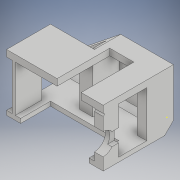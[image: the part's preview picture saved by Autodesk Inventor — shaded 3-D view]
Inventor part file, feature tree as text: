
AUTODESK INVENTOR PART (.ipt)
format: ipt  version: 2018 (Build 220112000, 112)  size: 257,024 bytes
history: native  units: in
note: dims shown in document units (in); Inventor stores cm internally (conversion verified against a paired STEP export)
features: extrude x12, sketch x12, projected_geometry x2
ambient origin geometry x8: Origin, YZ Plane, XZ Plane, XY Plane, X Axis, Y Axis, Z Axis, Center Point
bodies: Solid1 (feature_tree)
feature tree (26):
  extrude  "Extrusion1"  Depth=2.5591in
  extrude  "Extrusion2"  Depth=0.4921in
  sketch  "Sketch3"  dims[d5=0.2953in d6=0.1969in]
  extrude  "Extrusion4"  Depth=0.1969in
  extrude  "Extrusion5"  Depth=0.2953in
  sketch  "Sketch7"  dims[d11=4.3307in d12=0.0in d13=3.937in]
  extrude  "Extrusion6"  Depth=0.3937in
  extrude  "Extrusion7"  Depth=3.937in
  extrude  "Extrusion8"  Depth=1.1811in TaperAngle=0.0deg
  sketch  "Sketch9"  dims[d14=2.0669in d15=1.1811in d16=0.0in]
  extrude  "Extrusion11"  Depth=0.6299in
  extrude  "Extrusion12"  Depth=3.0709in
  sketch  "Sketch13"  dims[d26=1.1811in d27=0.0in d28=0.7087in]
  sketch  "Sketch14"  dims[d29=0.0591in d30=0.0in]
  extrude  "Extrusion13"  Depth=1.1811in
  extrude  "Extrusion14"  TaperAngle=0.0deg  [1 undecoded]
  extrude  "Extrusion15"  Depth=1.1811in TaperAngle=0.0deg
  sketch  "Sketch1"  dims[d0=3.1496in d1=2.5591in]
  sketch  "Sketch2"  dims[d3=0.5512in d4=0.4921in]
  sketch  "Sketch4"  dims[d7=0.689in d8=0.2953in]
  sketch  "Sketch5"  dims[d9=0.3937in d10=0.3937in]
  sketch  "Sketch11"  dims[d22=1.3386in d23=0.6299in]
  sketch  "Sketch12"  dims[d24=0.6299in d25=3.0709in]
  sketch  "Sketch15"  dims[d31=0.0591in d32=1.1811in d33=0.0in d39=1.5748in d40=0.9843in d41=1.9685in d43=0.1969in d44=0.1969in d45=0.1969in d46=1.1811in d47=0.0in d48=0.3937in d49=0.3937in d50=0.1969in d51=0.1969in d52=3.937in d53=0.0in d54=1.1811in d55=0.0in d56=0.5906in d57=0.9843in d62=0.1378in d63=1.1811in d64=0.3937in d65=1.1811in d66=0.0in d67=1.0827in d68=2.3622in d69=0.7874in d70=0.2953in d71=0.3937in d72=0.0in d73=0.3937in d74=0.0in d75=0.3937in d76=0.0in d77=0.2165in d78=0.0in]
  projected_geometry  "Projected Loop1"
  projected_geometry  "Projected Loop2"
note: 1 required parameter value undecoded (feature->parameter linkage not recoverable at this tier; creation-order binding heuristic only, values carry confidence <= 0.55)
